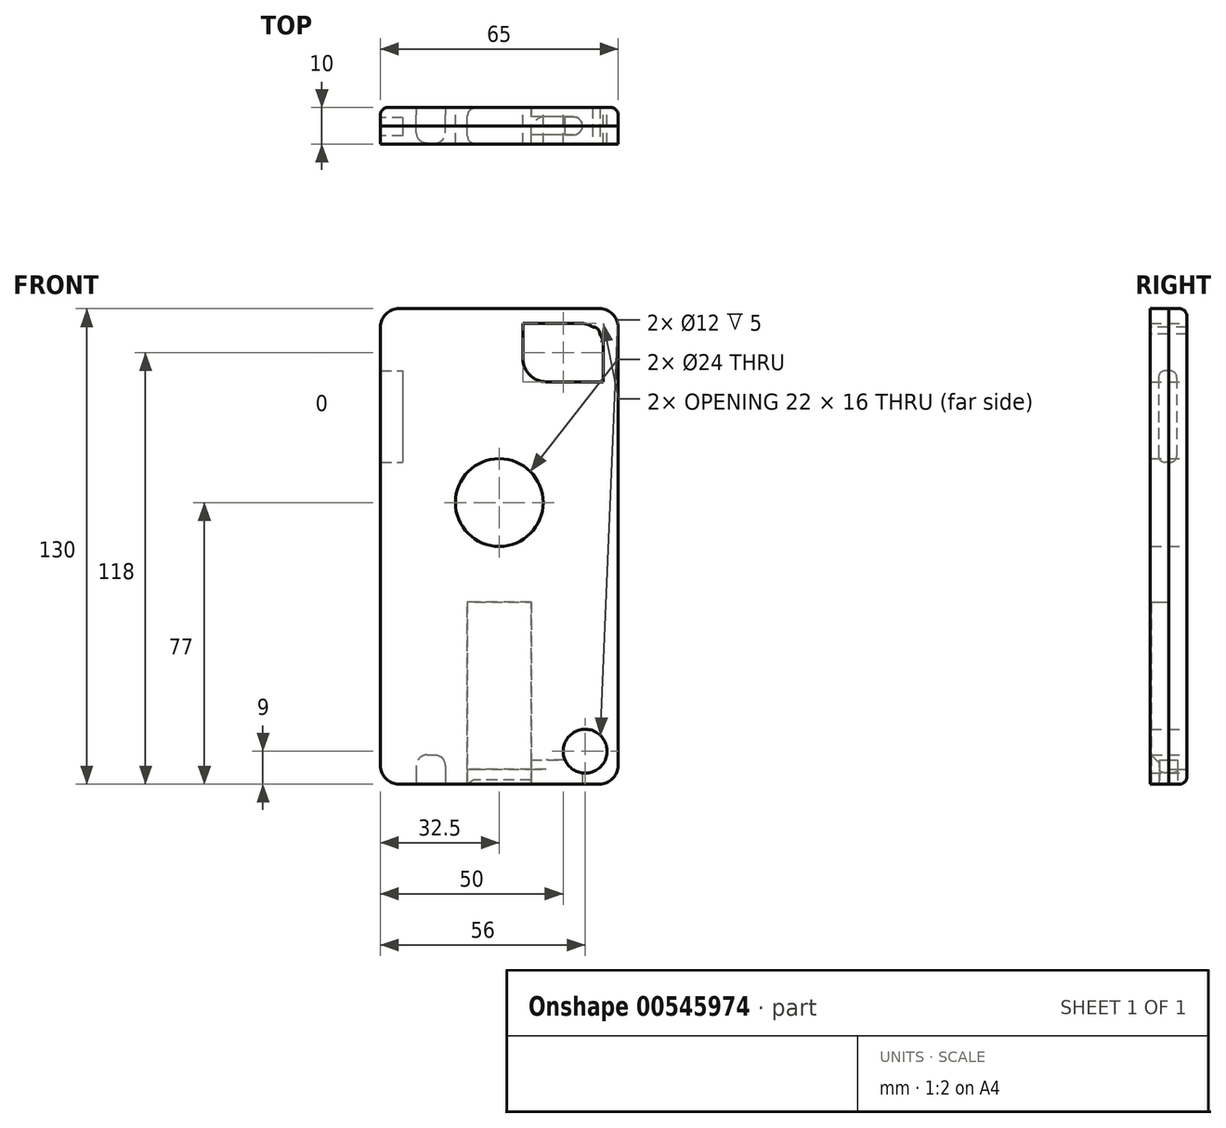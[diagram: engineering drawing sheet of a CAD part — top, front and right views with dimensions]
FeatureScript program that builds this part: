
annotation { "Feature Type Name" : "Feature", "Feature Type Description" : "" }
export const myFeature = defineFeature(function(context is Context, id is Id, definition is map)
    precondition{}
    {
        {
            var Q0;
            Q0=qCreatedBy(makeId("Front.planeOp"),FACE);
            var sketch = newSketch(context, id + "F0", { "sketchPlane" : qUnion([Q0])});
            skLineSegment(sketch, "E0.bottom", {"start": v(32.5, 65) * mm, "end": v(-32.5, 65) * mm});
            skLineSegment(sketch, "E0.top", {"start": v(32.5, -65) * mm, "end": v(-32.5, -65) * mm});
            skLineSegment(sketch, "E0.left", {"start": v(32.5, 65) * mm, "end": v(32.5, -65) * mm});
            skLineSegment(sketch, "E0.right", {"start": v(-32.5, 65) * mm, "end": v(-32.5, -65) * mm});
            skPoint(sketch, "E0.middle", {"position": v(0, 0) * mm});
            skSolve(sketch);
        }
        {
            var Q0;
            Q0=makeQuery(id+"F0.imprint","IMPRINT",FACE,{"disambiguationData":[TD([[makeQuery(id+"F0.imprint","IMPRINT",EDGE,{"derivedFrom":sQuery(id+"F0.wireOp",EDGE,"E0.bottom")}),1.0]])]});
            extrude(context, id + "F1", {"entities" : qUnion([Q0]), "depth" : 5 * mm, "offsetDistance" : 25.4 * mm});
        }
        {
            var Q0;
            Q0=makeQuery(id+"F1.opExtrude","CAP_FACE",FACE,{"disambiguationData":[OSD([sQuery(id+"F0.wireOp",EDGE,"E0.bottom"),sQuery(id+"F0.wireOp",EDGE,"E0.top"),sQuery(id+"F0.wireOp",EDGE,"E0.left"),sQuery(id+"F0.wireOp",EDGE,"E0.right")])],"isStart":true});
            extrude(context, id + "F2", {"entities" : qUnion([Q0]), "depth" : 5 * mm, "offsetDistance" : 25.4 * mm});
        }
        {
            var Q0;
            Q0=makeQuery(id+"F2.opExtrude","CAP_FACE",FACE,{"disambiguationData":[OSD([sQuery(id+"F0.wireOp",EDGE,"E0.bottom"),sQuery(id+"F0.wireOp",EDGE,"E0.top"),sQuery(id+"F0.wireOp",EDGE,"E0.left"),sQuery(id+"F0.wireOp",EDGE,"E0.right")])],"isStart":false});
            var sketch = newSketch(context, id + "F3", { "sketchPlane" : qUnion([Q0])});
            skCircle(sketch, "E1", {"center": v(0, 12) * mm, "radius": 12 * mm});
            skSolve(sketch);
        }
        {
            var Q0;
            Q0=makeQuery(id+"F3.imprint","IMPRINT",FACE,{"disambiguationData":[TD([[makeQuery(id+"F3.imprint","IMPRINT",EDGE,{"derivedFrom":sQuery(id+"F3.wireOp",EDGE,"E1")}),1.0]])]});
            extrude(context, id + "F4", {"entities" : qUnion([Q0]), "operationType" : NewBodyOperationType.REMOVE, "oppositeDirection" : true, "depth" : 25.4 * mm, "offsetDistance" : 25.4 * mm});
        }
        {
            var Q0;
            Q0=makeQuery(id+"F2.opExtrude","SWEPT_EDGE",EDGE,{"disambiguationData":[OSD([sQuery(id+"F0.wireOp",EDGE,"E0.bottom"),sQuery(id+"F0.wireOp",EDGE,"E0.right")])]});
            var Q1;
            Q1=makeQuery(id+"F1.opExtrude","SWEPT_EDGE",EDGE,{"disambiguationData":[OSD([sQuery(id+"F0.wireOp",EDGE,"E0.bottom"),sQuery(id+"F0.wireOp",EDGE,"E0.right")])]});
            var Q2;
            Q2=makeQuery(id+"F2.opExtrude","SWEPT_EDGE",EDGE,{"disambiguationData":[OSD([sQuery(id+"F0.wireOp",EDGE,"E0.top"),sQuery(id+"F0.wireOp",EDGE,"E0.right")])]});
            var Q3;
            Q3=makeQuery(id+"F1.opExtrude","SWEPT_EDGE",EDGE,{"disambiguationData":[OSD([sQuery(id+"F0.wireOp",EDGE,"E0.top"),sQuery(id+"F0.wireOp",EDGE,"E0.right")])]});
            var Q4;
            Q4=makeQuery(id+"F1.opExtrude","SWEPT_EDGE",EDGE,{"disambiguationData":[OSD([sQuery(id+"F0.wireOp",EDGE,"E0.bottom"),sQuery(id+"F0.wireOp",EDGE,"E0.left")])]});
            var Q5;
            Q5=makeQuery(id+"F1.opExtrude","SWEPT_EDGE",EDGE,{"disambiguationData":[OSD([sQuery(id+"F0.wireOp",EDGE,"E0.top"),sQuery(id+"F0.wireOp",EDGE,"E0.left")])]});
            var Q6;
            Q6=makeQuery(id+"F2.opExtrude","SWEPT_EDGE",EDGE,{"disambiguationData":[OSD([sQuery(id+"F0.wireOp",EDGE,"E0.top"),sQuery(id+"F0.wireOp",EDGE,"E0.left")])]});
            var Q7;
            Q7=makeQuery(id+"F2.opExtrude","SWEPT_EDGE",EDGE,{"disambiguationData":[OSD([sQuery(id+"F0.wireOp",EDGE,"E0.bottom"),sQuery(id+"F0.wireOp",EDGE,"E0.left")])]});
            fillet(context, id + "F5", {"entities" : qUnion([Q0, Q1, Q2, Q3, Q4, Q5, Q6, Q7]), "radius" : 5.08 * mm, "tangentPropagation" : true, "allowEdgeOverflow" : false});
        }
        {
            var Q0;
            Q0=makeQuery(id+"F2.opExtrude","CAP_FACE",FACE,{"disambiguationData":[OSD([sQuery(id+"F0.wireOp",EDGE,"E0.bottom"),sQuery(id+"F0.wireOp",EDGE,"E0.top"),sQuery(id+"F0.wireOp",EDGE,"E0.left"),sQuery(id+"F0.wireOp",EDGE,"E0.right")])],"isStart":false});
            var sketch = newSketch(context, id + "F6", { "sketchPlane" : qUnion([Q0])});
            skCircle(sketch, "E2", {"center": v(-23.5, -56) * mm, "radius": 6 * mm});
            skSolve(sketch);
        }
        {
            var Q0;
            Q0=makeQuery(id+"F6.imprint","IMPRINT",FACE,{"disambiguationData":[TD([[makeQuery(id+"F6.imprint","IMPRINT",EDGE,{"derivedFrom":sQuery(id+"F6.wireOp",EDGE,"E2")}),1.0]])]});
            extrude(context, id + "F7", {"entities" : qUnion([Q0]), "operationType" : NewBodyOperationType.REMOVE, "oppositeDirection" : true, "depth" : 25.4 * mm, "offsetDistance" : 25.4 * mm});
        }
        {
            var Q0;
            Q0=makeQuery(id+"F2.opExtrude","CAP_FACE",FACE,{"disambiguationData":[OSD([sQuery(id+"F0.wireOp",EDGE,"E0.bottom"),sQuery(id+"F0.wireOp",EDGE,"E0.top"),sQuery(id+"F0.wireOp",EDGE,"E0.left"),sQuery(id+"F0.wireOp",EDGE,"E0.right")])],"isStart":false});
            var sketch = newSketch(context, id + "F8", { "sketchPlane" : qUnion([Q0])});
            skLineSegment(sketch, "E3.bottom", {"start": v(-12.85, 45) * mm, "end": v(-28.5, 45) * mm});
            skLineSegment(sketch, "E3.top", {"start": v(-6.5, 61) * mm, "end": v(-22.15, 61) * mm});
            skLineSegment(sketch, "E3.left", {"start": v(-6.5, 51.35) * mm, "end": v(-6.5, 61) * mm});
            skLineSegment(sketch, "E3.right", {"start": v(-28.5, 45) * mm, "end": v(-28.5, 54.65) * mm});
            skPoint(sketch, "E3.middle", {"position": v(-19.83, 61.9) * mm});
            skPoint(sketch, "E4.visualSharp", {"position": v(-28.5, 61) * mm});
            skArc(sketch, "E4.filletArc", {"start": v(-22.15, 61) * mm, "mid": v(-26.64, 59.14) * mm, "end": v(-28.5, 54.65) * mm});
            skPoint(sketch, "E5.visualSharp", {"position": v(-6.5, 45) * mm});
            skArc(sketch, "E5.filletArc", {"start": v(-12.85, 45) * mm, "mid": v(-8.36, 46.86) * mm, "end": v(-6.5, 51.35) * mm});
            skSolve(sketch);
        }
        {
            var Q0;
            Q0=makeQuery(id+"F8.imprint","IMPRINT",FACE,{"disambiguationData":[TD([[makeQuery(id+"F8.imprint","IMPRINT",EDGE,{"derivedFrom":sQuery(id+"F8.wireOp",EDGE,"E3.bottom")}),-1.0]])]});
            extrude(context, id + "F9", {"entities" : qUnion([Q0]), "operationType" : NewBodyOperationType.REMOVE, "oppositeDirection" : true, "depth" : 25.4 * mm, "offsetDistance" : 25.4 * mm});
        }
        {
            var Q0;
            Q0=makeQuery(id+"F1.opExtrude","CAP_FACE",FACE,{"disambiguationData":[OSD([sQuery(id+"F0.wireOp",EDGE,"E0.bottom"),sQuery(id+"F0.wireOp",EDGE,"E0.top"),sQuery(id+"F0.wireOp",EDGE,"E0.left"),sQuery(id+"F0.wireOp",EDGE,"E0.right")])],"isStart":false});
            var sketch = newSketch(context, id + "F10", { "sketchPlane" : qUnion([Q0])});
            skLineSegment(sketch, "E6.bottom", {"start": v(-27.5, 60) * mm, "end": v(27.5, 60) * mm});
            skLineSegment(sketch, "E6.top", {"start": v(-27.5, -60) * mm, "end": v(27.5, -60) * mm});
            skLineSegment(sketch, "E6.left", {"start": v(-27.5, 60) * mm, "end": v(-27.5, -60) * mm});
            skLineSegment(sketch, "E6.right", {"start": v(27.5, 60) * mm, "end": v(27.5, -60) * mm});
            skSolve(sketch);
        }
        {
            var Q0;
            Q0=makeQuery(id+"F10.imprint","IMPRINT",FACE,{"disambiguationData":[TD([[makeQuery(id+"F10.imprint","IMPRINT",EDGE,{"derivedFrom":sQuery(id+"F10.wireOp",EDGE,"E6.bottom")}),-1.0]])]});
            extrude(context, id + "F11", {"entities" : qUnion([Q0]), "operationType" : NewBodyOperationType.REMOVE, "oppositeDirection" : true, "depth" : 25.4 * mm, "offsetDistance" : 25.4 * mm});
        }
        {
            var Q0;
            Q0=makeQuery(id+"F11.boolean.opBoolean","COPY",EDGE,{"derivedFrom":makeQuery(id+"F11.opExtrude","SWEPT_EDGE",EDGE,{"disambiguationData":[OSD([sQuery(id+"F10.wireOp",EDGE,"E6.bottom"),sQuery(id+"F10.wireOp",EDGE,"E6.right")])]})});
            var Q1;
            Q1=makeQuery(id+"F11.boolean.opBoolean","COPY",EDGE,{"derivedFrom":makeQuery(id+"F11.opExtrude","SWEPT_EDGE",EDGE,{"disambiguationData":[OSD([sQuery(id+"F10.wireOp",EDGE,"E6.bottom"),sQuery(id+"F10.wireOp",EDGE,"E6.left")])]})});
            var Q2;
            Q2=makeQuery(id+"F11.boolean.opBoolean","COPY",EDGE,{"derivedFrom":makeQuery(id+"F11.opExtrude","SWEPT_EDGE",EDGE,{"disambiguationData":[OSD([sQuery(id+"F10.wireOp",EDGE,"E6.top"),sQuery(id+"F10.wireOp",EDGE,"E6.left")])]})});
            var Q3;
            Q3=makeQuery(id+"F11.boolean.opBoolean","COPY",EDGE,{"derivedFrom":makeQuery(id+"F11.opExtrude","SWEPT_EDGE",EDGE,{"disambiguationData":[OSD([sQuery(id+"F10.wireOp",EDGE,"E6.top"),sQuery(id+"F10.wireOp",EDGE,"E6.right")])]})});
            fillet(context, id + "F12", {"entities" : qUnion([Q0, Q1, Q2, Q3]), "radius" : 1.84 * mm, "tangentPropagation" : true, "allowEdgeOverflow" : false});
        }
        {
            var Q0;
            Q0=makeQuery(id+"F1.opExtrude","SWEPT_FACE",FACE,{"disambiguationData":[OSD([sQuery(id+"F0.wireOp",EDGE,"E0.top")])]});
            var sketch = newSketch(context, id + "F13", { "sketchPlane" : qUnion([Q0])});
            skLineSegment(sketch, "E7.bottom", {"start": v(-8.7, 4.8) * mm, "end": v(8.7, 4.8) * mm});
            skLineSegment(sketch, "E7.top", {"start": v(-8.7, 0) * mm, "end": v(8.7, 0) * mm});
            skLineSegment(sketch, "E7.left", {"start": v(-8.7, 4.8) * mm, "end": v(-8.7, 0) * mm});
            skLineSegment(sketch, "E7.right", {"start": v(8.7, 4.8) * mm, "end": v(8.7, 0) * mm});
            skPoint(sketch, "E7.middle", {"position": v(0, 2.5) * mm});
            skSolve(sketch);
        }
        {
            var Q0;
            Q0=makeQuery(id+"F13.imprint","IMPRINT",FACE,{"disambiguationData":[TD([[makeQuery(id+"F13.imprint","IMPRINT",EDGE,{"derivedFrom":sQuery(id+"F13.wireOp",EDGE,"E7.bottom")}),-1.0]])]});
            extrude(context, id + "F14", {"entities" : qUnion([Q0]), "operationType" : NewBodyOperationType.REMOVE, "oppositeDirection" : true, "depth" : 49.78 * mm, "offsetDistance" : 25.4 * mm});
        }
        {
            var Q0;
            Q0=makeQuery(id+"F2.opExtrude","SWEPT_FACE",FACE,{"disambiguationData":[OSD([sQuery(id+"F0.wireOp",EDGE,"E0.top")])]});
            var sketch = newSketch(context, id + "F15", { "sketchPlane" : qUnion([Q0])});
            skLineSegment(sketch, "E8.bottom", {"start": v(-8.7, 0) * mm, "end": v(8.7, 0) * mm});
            skLineSegment(sketch, "E8.top", {"start": v(-8.7, -4.8) * mm, "end": v(8.7, -4.8) * mm});
            skLineSegment(sketch, "E8.left", {"start": v(-8.7, 0) * mm, "end": v(-8.7, -4.8) * mm});
            skLineSegment(sketch, "E8.right", {"start": v(8.7, 0) * mm, "end": v(8.7, -4.8) * mm});
            skSolve(sketch);
        }
        {
            var Q0;
            Q0=makeQuery(id+"F15.imprint","IMPRINT",FACE,{"disambiguationData":[TD([[makeQuery(id+"F15.imprint","IMPRINT",EDGE,{"derivedFrom":sQuery(id+"F15.wireOp",EDGE,"E8.bottom")}),1.0]])]});
            var Q1;
            Q1=qSketchRegion(id+"F24",true);
            extrude(context, id + "F16", {"entities" : qUnion([Q0, Q1]), "operationType" : NewBodyOperationType.REMOVE, "oppositeDirection" : true, "depth" : 4.06 * mm, "offsetDistance" : 25.4 * mm});
        }
        {
            var Q0;
            Q0=makeQuery(id+"F2.opExtrude","CAP_EDGE",EDGE,{"disambiguationData":[OSD([sQuery(id+"F0.wireOp",EDGE,"E0.right")])],"isStart":false});
            fillet(context, id + "F17", {"entities" : qUnion([Q0]), "radius" : 2 * mm, "tangentPropagation" : true, "allowEdgeOverflow" : false});
        }
        {
            var Q0;
            Q0=makeQuery(id+"F2.opExtrude","SWEPT_FACE",FACE,{"disambiguationData":[OSD([sQuery(id+"F0.wireOp",EDGE,"E0.right")])]});
            var sketch = newSketch(context, id + "F18", { "sketchPlane" : qUnion([Q0])});
            skLineSegment(sketch, "E9.bottom", {"start": v(-2.23, 48) * mm, "end": v(2.77, 48) * mm});
            skLineSegment(sketch, "E9.top", {"start": v(-2.23, 23) * mm, "end": v(2.77, 23) * mm});
            skLineSegment(sketch, "E9.left", {"start": v(-2.23, 48) * mm, "end": v(-2.23, 23) * mm});
            skLineSegment(sketch, "E9.right", {"start": v(2.77, 48) * mm, "end": v(2.77, 23) * mm});
            skSolve(sketch);
        }
        {
            var Q0;
            {var subQ0=sQuery(id+"F18.wireOp",EDGE,"E9.right");Q0=makeQuery(id+"F18.imprint","IMPRINT",FACE,{"disambiguationData":[TD([[makeQuery(id+"F18.imprint","IMPRINT",EDGE,{"derivedFrom":subQ0}),-1.0]])]});}
            var Q1;
            {var subQ0=sQuery(id+"F18.wireOp",EDGE,"E9.left");Q1=makeQuery(id+"F18.imprint","IMPRINT",FACE,{"disambiguationData":[TD([[makeQuery(id+"F18.imprint","IMPRINT",EDGE,{"derivedFrom":subQ0}),1.0]])]});}
            extrude(context, id + "F19", {"entities" : qUnion([Q0, Q1]), "operationType" : NewBodyOperationType.REMOVE, "oppositeDirection" : true, "depth" : 6.1 * mm, "offsetDistance" : 25.4 * mm});
        }
        {
            var Q0;
            Q0=makeQuery(id+"F19.boolean.opBoolean","COPY",EDGE,{"derivedFrom":makeQuery(id+"F19.opExtrude","SWEPT_EDGE",EDGE,{"disambiguationData":[OSD([sQuery(id+"F18.wireOp",EDGE,"E9.bottom"),sQuery(id+"F18.wireOp",EDGE,"E9.right")])]})});
            var Q1;
            Q1=makeQuery(id+"F19.boolean.opBoolean","COPY",EDGE,{"derivedFrom":makeQuery(id+"F19.opExtrude","SWEPT_EDGE",EDGE,{"disambiguationData":[OSD([sQuery(id+"F18.wireOp",EDGE,"E9.bottom"),sQuery(id+"F18.wireOp",EDGE,"E9.left")])]})});
            var Q2;
            Q2=makeQuery(id+"F19.boolean.opBoolean","COPY",EDGE,{"derivedFrom":makeQuery(id+"F19.opExtrude","SWEPT_EDGE",EDGE,{"disambiguationData":[OSD([sQuery(id+"F18.wireOp",EDGE,"E9.top"),sQuery(id+"F18.wireOp",EDGE,"E9.left")])]})});
            var Q3;
            Q3=makeQuery(id+"F19.boolean.opBoolean","COPY",EDGE,{"derivedFrom":makeQuery(id+"F19.opExtrude","SWEPT_EDGE",EDGE,{"disambiguationData":[OSD([sQuery(id+"F18.wireOp",EDGE,"E9.top"),sQuery(id+"F18.wireOp",EDGE,"E9.right")])]})});
            fillet(context, id + "F20", {"entities" : qUnion([Q0, Q1, Q2, Q3]), "radius" : 1.84 * mm, "tangentPropagation" : true, "allowEdgeOverflow" : false});
        }
        {
            var Q0;
            Q0=makeQuery(id+"F17.opFillet","SPLIT",FACE,{"disambiguationData":[OD(1.0)],"derivedFrom":makeQuery(id+"F2.opExtrude","SWEPT_FACE",FACE,{"disambiguationData":[OSD([sQuery(id+"F0.wireOp",EDGE,"E0.top")])]})});
            var sketch = newSketch(context, id + "F21", { "sketchPlane" : qUnion([Q0])});
            skLineSegment(sketch, "E10.bottom", {"start": v(-22.7, 4.8) * mm, "end": v(-14.7, 4.8) * mm});
            skLineSegment(sketch, "E10.top", {"start": v(-22.7, -5) * mm, "end": v(-14.7, -5) * mm});
            skLineSegment(sketch, "E10.left", {"start": v(-22.7, 4.8) * mm, "end": v(-22.7, -5) * mm});
            skLineSegment(sketch, "E10.right", {"start": v(-14.7, 4.8) * mm, "end": v(-14.7, -5) * mm});
            skSolve(sketch);
        }
        {
            var Q0;
            {var subQ0=sQuery(id+"F21.wireOp",EDGE,"E10.left");var subQ1=sQuery(id+"F0.wireOp",EDGE,"E0.top");var subQ2=makeQuery(id+"F2.opExtrude","SWEPT_FACE",FACE,{"disambiguationData":[OSD([subQ1])]});var subQ6=makeQuery(id+"F17.opFillet","BLEND_EDGE",EDGE,{"disambiguationData":[OD(1.0)],"blendedFrom":[makeQuery(id+"F2.opExtrude","CAP_EDGE",EDGE,{"disambiguationData":[OSD([subQ1])],"isStart":false}),subQ2],"blendedInto":[subQ2]});var subQ7=makeQuery(id+"F21.imprint","INTERSECT",VERTEX,{"derivedFrom":[subQ6,subQ0]});Q0=makeQuery(id+"F21.imprint","IMPRINT",FACE,{"disambiguationData":[TD([[makeQuery(id+"F21.imprint","IMPRINT",EDGE,{"disambiguationData":[TD([[subQ7,-1.0]])],"derivedFrom":subQ6}),1.0]])]});}
            var Q1;
            {var subQ0=sQuery(id+"F21.wireOp",EDGE,"E10.top");Q1=makeQuery(id+"F21.imprint","IMPRINT",FACE,{"disambiguationData":[TD([[makeQuery(id+"F21.imprint","IMPRINT",EDGE,{"derivedFrom":subQ0}),1.0]])]});}
            var Q2;
            {var subQ0=sQuery(id+"F21.wireOp",EDGE,"E10.bottom");Q2=makeQuery(id+"F21.imprint","IMPRINT",FACE,{"disambiguationData":[TD([[makeQuery(id+"F21.imprint","IMPRINT",EDGE,{"derivedFrom":subQ0}),-1.0]])]});}
            extrude(context, id + "F22", {"entities" : qUnion([Q0, Q1, Q2]), "operationType" : NewBodyOperationType.REMOVE, "oppositeDirection" : true, "depth" : 8 * mm, "offsetDistance" : 25.4 * mm});
        }
        {
            var Q0;
            Q0=makeQuery(id+"F22.boolean.opBoolean","COPY",EDGE,{"derivedFrom":makeQuery(id+"F22.opExtrude","CAP_EDGE",EDGE,{"disambiguationData":[OSD([sQuery(id+"F21.wireOp",EDGE,"E10.left")])],"isStart":false})});
            var Q1;
            Q1=makeQuery(id+"F22.boolean.opBoolean","COPY",EDGE,{"derivedFrom":makeQuery(id+"F22.opExtrude","CAP_EDGE",EDGE,{"disambiguationData":[OSD([sQuery(id+"F21.wireOp",EDGE,"E10.right")])],"isStart":false})});
            var Q2;
            Q2=makeQuery(id+"F22.boolean.opBoolean","COPY",EDGE,{"derivedFrom":makeQuery(id+"F22.opExtrude","SWEPT_EDGE",EDGE,{"disambiguationData":[OSD([sQuery(id+"F21.wireOp",EDGE,"E10.bottom"),sQuery(id+"F21.wireOp",EDGE,"E10.right")])]})});
            var Q3;
            Q3=makeQuery(id+"F22.boolean.opBoolean","COPY",EDGE,{"derivedFrom":makeQuery(id+"F22.opExtrude","SWEPT_EDGE",EDGE,{"disambiguationData":[OSD([sQuery(id+"F21.wireOp",EDGE,"E10.bottom"),sQuery(id+"F21.wireOp",EDGE,"E10.left")])]})});
            fillet(context, id + "F23", {"entities" : qUnion([Q0, Q1, Q2, Q3]), "radius" : 3 * mm, "tangentPropagation" : true, "allowEdgeOverflow" : false});
        }
        {
            var Q0;
            Q0=makeQuery(id+"F17.opFillet","SPLIT",FACE,{"disambiguationData":[OD(0.0)],"derivedFrom":makeQuery(id+"F2.opExtrude","SWEPT_FACE",FACE,{"disambiguationData":[OSD([sQuery(id+"F0.wireOp",EDGE,"E0.top")])]})});
            var sketch = newSketch(context, id + "F24", { "sketchPlane" : qUnion([Q0])});
            skLineSegment(sketch, "E11.bottom", {"start": v(22.7, 2.5) * mm, "end": v(8.7, 2.5) * mm});
            skLineSegment(sketch, "E11.top", {"start": v(22.7, -2.5) * mm, "end": v(8.7, -2.5) * mm});
            skLineSegment(sketch, "E11.left", {"start": v(22.7, 2.5) * mm, "end": v(22.7, -2.5) * mm});
            skLineSegment(sketch, "E11.right", {"start": v(8.7, 2.5) * mm, "end": v(8.7, -2.5) * mm});
            skPoint(sketch, "E11.middle", {"position": v(11.73, 0) * mm});
            skSolve(sketch);
        }
        {
            var Q0;
            {var subQ0=sQuery(id+"F24.wireOp",EDGE,"E11.bottom");Q0=makeQuery(id+"F24.imprint","IMPRINT",FACE,{"disambiguationData":[TD([[makeQuery(id+"F24.imprint","IMPRINT",EDGE,{"derivedFrom":subQ0}),1.0]])]});}
            var Q1;
            {var subQ0=sQuery(id+"F24.wireOp",EDGE,"E11.top");Q1=makeQuery(id+"F24.imprint","IMPRINT",FACE,{"disambiguationData":[TD([[makeQuery(id+"F24.imprint","IMPRINT",EDGE,{"derivedFrom":subQ0}),-1.0]])]});}
            extrude(context, id + "F25", {"entities" : qUnion([Q0, Q1]), "operationType" : NewBodyOperationType.REMOVE, "oppositeDirection" : true, "depth" : 6.6 * mm, "offsetDistance" : 25.4 * mm});
        }
        {
            var Q0;
            Q0=makeQuery(id+"F25.boolean.opBoolean","COPY",EDGE,{"derivedFrom":makeQuery(id+"F25.opExtrude","SWEPT_EDGE",EDGE,{"disambiguationData":[OSD([sQuery(id+"F24.wireOp",EDGE,"E11.bottom"),sQuery(id+"F24.wireOp",EDGE,"E11.left")])]})});
            var Q1;
            Q1=makeQuery(id+"F25.boolean.opBoolean","COPY",EDGE,{"derivedFrom":makeQuery(id+"F25.opExtrude","SWEPT_EDGE",EDGE,{"disambiguationData":[OSD([sQuery(id+"F24.wireOp",EDGE,"E11.top"),sQuery(id+"F24.wireOp",EDGE,"E11.left")])]})});
            fillet(context, id + "F26", {"entities" : qUnion([Q0, Q1]), "radius" : 2.45 * mm, "tangentPropagation" : true, "allowEdgeOverflow" : false});
        }
        {
            var Q0;
            {var subQ0=sQuery(id+"F15.wireOp",EDGE,"E8.right");var subQ1=sQuery(id+"F24.wireOp",EDGE,"E11.top");Q0=makeQuery(id+"F25.boolean.opBoolean","COPY",EDGE,{"disambiguationData":[topologyDisambiguationEdgeConnected([makeQuery(id+"F16.boolean.opBoolean","COPY",FACE,{"derivedFrom":makeQuery(id+"F16.opExtrude","SWEPT_FACE",FACE,{"disambiguationData":[OSD([subQ0])]})})])],"derivedFrom":makeQuery(id+"F25.opExtrude","SWEPT_EDGE",EDGE,{"disambiguationData":[OSD([subQ0,subQ1,sQuery(id+"F24.wireOp",EDGE,"E11.right")])]})});}
            var Q1;
            Q1=makeQuery(id+"F25.boolean.opBoolean","COPY",EDGE,{"derivedFrom":makeQuery(id+"F25.opExtrude","SWEPT_EDGE",EDGE,{"disambiguationData":[OSD([sQuery(id+"F24.wireOp",EDGE,"E11.bottom"),sQuery(id+"F24.wireOp",EDGE,"E11.right")])]})});
            fillet(context, id + "F27", {"entities" : qUnion([Q0, Q1]), "radius" : 4.54 * mm, "tangentPropagation" : true, "allowEdgeOverflow" : false});
        }
        {
            var Q0;
            Q0=makeQuery(id+"F14.boolean.opBoolean","COPY",EDGE,{"derivedFrom":makeQuery(id+"F14.opExtrude","SWEPT_EDGE",EDGE,{"disambiguationData":[OSD([sQuery(id+"F13.wireOp",EDGE,"E7.bottom"),sQuery(id+"F13.wireOp",EDGE,"E7.left")])]})});
            var Q1;
            Q1=makeQuery(id+"F16.boolean.opBoolean","COPY",EDGE,{"derivedFrom":makeQuery(id+"F16.opExtrude","SWEPT_EDGE",EDGE,{"disambiguationData":[OSD([sQuery(id+"F15.wireOp",EDGE,"E8.top"),sQuery(id+"F15.wireOp",EDGE,"E8.left")])]})});
            fillet(context, id + "F28", {"entities" : qUnion([Q0, Q1]), "radius" : 2.02 * mm, "tangentPropagation" : true, "allowEdgeOverflow" : false});
        }
        {
            var Q0;
            Q0=qCreatedBy(makeId("Front.planeOp"),FACE);
            cPlane(context, id + "F29", {"entities" : qUnion([Q0]), "cplaneType" : CPlaneType.OFFSET, "offset" : 5 * mm, "width" : 152.4 * mm, "height" : 152.4 * mm});
        }
    });
